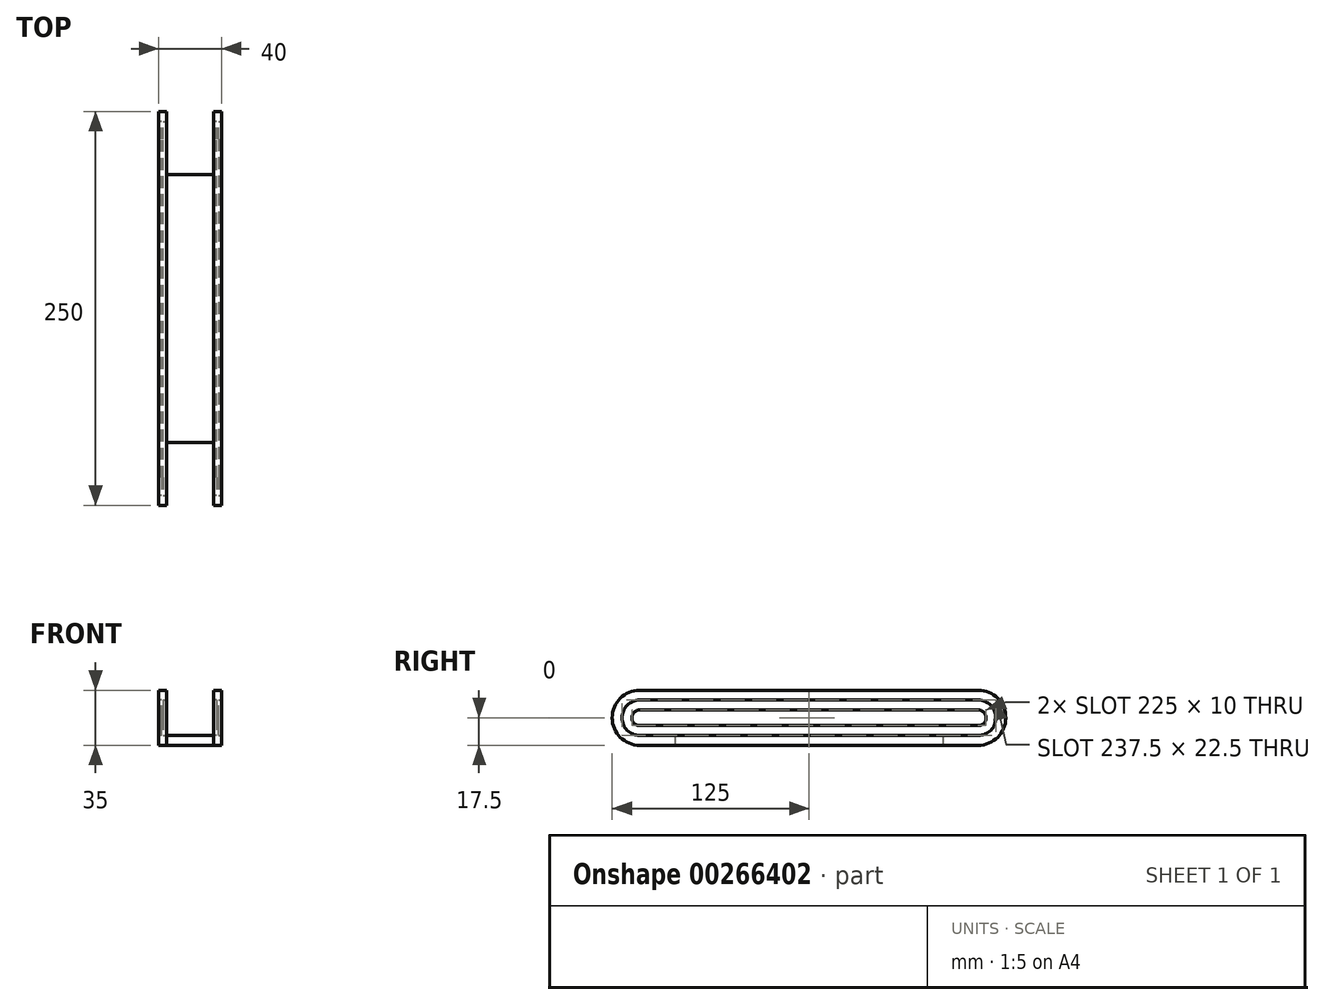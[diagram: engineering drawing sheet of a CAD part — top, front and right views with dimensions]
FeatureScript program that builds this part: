
annotation { "Feature Type Name" : "Feature", "Feature Type Description" : "" }
export const myFeature = defineFeature(function(context is Context, id is Id, definition is map)
    precondition{}
    {
        {
            var Q0;
            Q0=qCreatedBy(makeId("Front.planeOp"),FACE);
            var sketch = newSketch(context, id + "F0", { "sketchPlane" : qUnion([Q0])});
            skLineSegment(sketch, "E0.bottom", {"start": v(20, -17.5) * mm, "end": v(-20, -17.5) * mm});
            skLineSegment(sketch, "E0.left", {"start": v(20, -17.5) * mm, "end": v(20, 17.5) * mm});
            skLineSegment(sketch, "E0.right", {"start": v(-20, -17.5) * mm, "end": v(-20, 17.5) * mm});
            skPoint(sketch, "E0.middle", {"position": v(0, 0) * mm});
            skLineSegment(sketch, "E1", {"start": v(-20, 17.5) * mm, "end": v(-15, 17.5) * mm});
            skLineSegment(sketch, "E2", {"start": v(20, 17.5) * mm, "end": v(15, 17.5) * mm});
            skLineSegment(sketch, "E3", {"start": v(-15, 17.5) * mm, "end": v(-15, -11.25) * mm});
            skLineSegment(sketch, "E4", {"start": v(-15, -11.25) * mm, "end": v(15, -11.25) * mm});
            skLineSegment(sketch, "E5", {"start": v(15, -11.25) * mm, "end": v(15, 17.5) * mm});
            skSolve(sketch);
        }
        {
            var Q0;
            Q0=makeQuery(id+"F0.imprint","IMPRINT",FACE,{"disambiguationData":[TD([[makeQuery(id+"F0.imprint","IMPRINT",EDGE,{"derivedFrom":sQuery(id+"F0.wireOp",EDGE,"E0.bottom")}),-1.0]])]});
            extrude(context, id + "F1", {"entities" : qUnion([Q0]), "depth" : 125 * mm, "hasSecondDirection" : true, "secondDirectionOppositeDirection" : true, "secondDirectionDepth" : 125 * mm});
        }
        {
            var Q0;
            Q0=makeQuery(id+"F1.opExtrude","SWEPT_FACE",FACE,{"disambiguationData":[OSD([sQuery(id+"F0.wireOp",EDGE,"E3")])]});
            var sketch = newSketch(context, id + "F2", { "sketchPlane" : qUnion([Q0])});
            skLineSegment(sketch, "E6", {"start": v(0, 11.25) * mm, "end": v(-107.5, 11.25) * mm});
            skLineSegment(sketch, "E7", {"start": v(0, 5) * mm, "end": v(-107.5, 5) * mm});
            skLineSegment(sketch, "E8", {"start": v(0, -11.25) * mm, "end": v(-107.5, -11.25) * mm});
            skLineSegment(sketch, "E9", {"start": v(0, -5) * mm, "end": v(-107.5, -5) * mm});
            skArc(sketch, "E10", {"start": v(-107.5, 11.25) * mm, "mid": v(-118.75, 0) * mm, "end": v(-107.5, -11.25) * mm});
            skArc(sketch, "E11", {"start": v(-107.5, 5) * mm, "mid": v(-112.5, 0) * mm, "end": v(-107.5, -5) * mm});
            skLineSegment(sketch, "E12", {"start": v(0, 11.25) * mm, "end": v(107.5, 11.25) * mm});
            skLineSegment(sketch, "E13", {"start": v(0, -11.25) * mm, "end": v(107.5, -11.25) * mm});
            skLineSegment(sketch, "E14", {"start": v(0, -5) * mm, "end": v(107.5, -5) * mm});
            skLineSegment(sketch, "E15", {"start": v(0, 5) * mm, "end": v(107.5, 5) * mm});
            skArc(sketch, "E16", {"start": v(107.5, -11.25) * mm, "mid": v(118.75, 0) * mm, "end": v(107.5, 11.25) * mm});
            skArc(sketch, "E17", {"start": v(107.5, -5) * mm, "mid": v(112.5, 0) * mm, "end": v(107.5, 5) * mm});
            skSolve(sketch);
        }
        {
            var Q0;
            Q0=makeQuery(id+"F1.opExtrude","SWEPT_FACE",FACE,{"disambiguationData":[OSD([sQuery(id+"F0.wireOp",EDGE,"E5")])]});
            var sketch = newSketch(context, id + "F3", { "sketchPlane" : qUnion([Q0])});
            skPoint(sketch, "E18.endSnap0", {"position": v(0, 17.5) * mm});
            skPoint(sketch, "E19.endSnap0", {"position": v(0, -11.25) * mm});
            skLineSegment(sketch, "E20", {"start": v(0, 5) * mm, "end": v(-107.5, 5) * mm});
            skLineSegment(sketch, "E21", {"start": v(0, -5) * mm, "end": v(-107.5, -5) * mm});
            skLineSegment(sketch, "E22", {"start": v(0, 5) * mm, "end": v(107.5, 5) * mm});
            skLineSegment(sketch, "E23", {"start": v(0, -5) * mm, "end": v(107.5, -5) * mm});
            skLineSegment(sketch, "E24", {"start": v(0, 11.25) * mm, "end": v(107.5, 11.25) * mm});
            skLineSegment(sketch, "E25", {"start": v(0, -11.25) * mm, "end": v(107.5, -11.25) * mm});
            skLineSegment(sketch, "E26", {"start": v(0, 11.25) * mm, "end": v(-107.5, 11.25) * mm});
            skLineSegment(sketch, "E27", {"start": v(0, -11.25) * mm, "end": v(-107.5, -11.25) * mm});
            skArc(sketch, "E28", {"start": v(-107.5, 5) * mm, "mid": v(-112.5, 0) * mm, "end": v(-107.5, -5) * mm});
            skArc(sketch, "E29", {"start": v(-107.5, 11.25) * mm, "mid": v(-118.75, 0) * mm, "end": v(-107.5, -11.25) * mm});
            skPoint(sketch, "E30.end.orphan", {"position": v(125, 3.13) * mm});
            skPoint(sketch, "E30.start.orphan", {"position": v(0, 0) * mm});
            skArc(sketch, "E31", {"start": v(107.5, -5) * mm, "mid": v(112.5, 0) * mm, "end": v(107.5, 5) * mm});
            skArc(sketch, "E32", {"start": v(107.5, -11.25) * mm, "mid": v(118.75, 0) * mm, "end": v(107.5, 11.25) * mm});
            skPoint(sketch, "E19.start.orphan", {"position": v(0, -11.25) * mm});
            skSolve(sketch);
        }
        {
            var Q0;
            Q0=makeQuery(id+"F1.opExtrude","SWEPT_FACE",FACE,{"disambiguationData":[OSD([sQuery(id+"F0.wireOp",EDGE,"E0.right")])]});
            var sketch = newSketch(context, id + "F4", { "sketchPlane" : qUnion([Q0])});
            skPoint(sketch, "E33.endSnap0", {"position": v(0, 17.5) * mm});
            skLineSegment(sketch, "E34", {"start": v(0, 11.25) * mm, "end": v(-107.5, 11.25) * mm});
            skLineSegment(sketch, "E35", {"start": v(0, -11.25) * mm, "end": v(-107.5, -11.25) * mm});
            skLineSegment(sketch, "E36", {"start": v(0, 5) * mm, "end": v(-107.5, 5) * mm});
            skLineSegment(sketch, "E37", {"start": v(0, -5) * mm, "end": v(-107.5, -5) * mm});
            skLineSegment(sketch, "E38", {"start": v(0, 11.25) * mm, "end": v(107.5, 11.25) * mm});
            skLineSegment(sketch, "E39", {"start": v(0, 5) * mm, "end": v(107.5, 5) * mm});
            skLineSegment(sketch, "E40", {"start": v(0, -5) * mm, "end": v(107.5, -5) * mm});
            skLineSegment(sketch, "E41", {"start": v(0, -11.25) * mm, "end": v(107.5, -11.25) * mm});
            skArc(sketch, "E42", {"start": v(107.5, -5) * mm, "mid": v(112.5, 0) * mm, "end": v(107.5, 5) * mm});
            skArc(sketch, "E43", {"start": v(107.5, -11.25) * mm, "mid": v(118.75, 0) * mm, "end": v(107.5, 11.25) * mm});
            skArc(sketch, "E44", {"start": v(-107.5, 5) * mm, "mid": v(-112.5, 0) * mm, "end": v(-107.5, -5) * mm});
            skArc(sketch, "E45", {"start": v(-107.5, 11.25) * mm, "mid": v(-118.75, 0) * mm, "end": v(-107.5, -11.25) * mm});
            skPoint(sketch, "E46.orphan", {"position": v(-125, 0) * mm});
            skPoint(sketch, "E47.orphan", {"position": v(-125, -5) * mm});
            skPoint(sketch, "E48.start.orphan", {"position": v(-125, 5) * mm});
            skPoint(sketch, "E49.orphan", {"position": v(125, 0) * mm});
            skPoint(sketch, "E50.end.orphan", {"position": v(125, -5) * mm});
            skPoint(sketch, "E51.orphan", {"position": v(125, 5) * mm});
            skSolve(sketch);
        }
        {
            var Q0;
            Q0=makeQuery(id+"F1.opExtrude","SWEPT_FACE",FACE,{"disambiguationData":[OSD([sQuery(id+"F0.wireOp",EDGE,"E0.left")])]});
            var sketch = newSketch(context, id + "F5", { "sketchPlane" : qUnion([Q0])});
            skLineSegment(sketch, "E52", {"start": v(0, 11.25) * mm, "end": v(-107.5, 11.25) * mm});
            skLineSegment(sketch, "E53", {"start": v(0, -11.25) * mm, "end": v(-107.5, -11.25) * mm});
            skLineSegment(sketch, "E54", {"start": v(0, 11.25) * mm, "end": v(107.5, 11.25) * mm});
            skLineSegment(sketch, "E55", {"start": v(0, -11.25) * mm, "end": v(107.5, -11.25) * mm});
            skLineSegment(sketch, "E56", {"start": v(0, 5) * mm, "end": v(107.5, 5) * mm});
            skLineSegment(sketch, "E57", {"start": v(0, -5) * mm, "end": v(107.5, -5) * mm});
            skLineSegment(sketch, "E58", {"start": v(0, 5) * mm, "end": v(-107.5, 5) * mm});
            skLineSegment(sketch, "E59", {"start": v(0, -5) * mm, "end": v(-107.5, -5) * mm});
            skArc(sketch, "E60", {"start": v(107.5, -5) * mm, "mid": v(112.5, 0) * mm, "end": v(107.5, 5) * mm});
            skArc(sketch, "E61", {"start": v(107.5, -11.25) * mm, "mid": v(118.75, 0) * mm, "end": v(107.5, 11.25) * mm});
            skArc(sketch, "E62", {"start": v(-107.5, 5) * mm, "mid": v(-112.5, 0) * mm, "end": v(-107.5, -5) * mm});
            skArc(sketch, "E63", {"start": v(-107.5, 11.25) * mm, "mid": v(-118.75, 0) * mm, "end": v(-107.5, -11.25) * mm});
            skPoint(sketch, "E64.orphan", {"position": v(-125, 5) * mm});
            skPoint(sketch, "E65.start.orphan", {"position": v(-125, 0) * mm});
            skPoint(sketch, "E66.orphan", {"position": v(-125, -5) * mm});
            skPoint(sketch, "E67.start.orphan", {"position": v(0, 17.5) * mm});
            skPoint(sketch, "E68.start.orphan", {"position": v(125, 2.5) * mm});
            skPoint(sketch, "E69.orphan", {"position": v(125, 7.5) * mm});
            skPoint(sketch, "E70.end.orphan", {"position": v(125, -2.5) * mm});
            skSolve(sketch);
        }
        {
            var Q0;
            Q0=makeQuery(id+"F3.imprint","IMPRINT",FACE,{"disambiguationData":[TD([[makeQuery(id+"F3.imprint","IMPRINT",EDGE,{"derivedFrom":sQuery(id+"F3.wireOp",EDGE,"E20")}),1.0]])]});
            extrude(context, id + "F6", {"entities" : qUnion([Q0]), "operationType" : NewBodyOperationType.REMOVE, "endBound" : BoundingType.THROUGH_ALL, "oppositeDirection" : true, "depth" : 25 * mm});
        }
        {
            var Q0;
            Q0=makeQuery(id+"F2.imprint","IMPRINT",FACE,{"disambiguationData":[TD([[makeQuery(id+"F2.imprint","IMPRINT",EDGE,{"derivedFrom":sQuery(id+"F2.wireOp",EDGE,"E7")}),1.0]])]});
            extrude(context, id + "F7", {"entities" : qUnion([Q0]), "operationType" : NewBodyOperationType.REMOVE, "endBound" : BoundingType.THROUGH_ALL, "oppositeDirection" : true, "depth" : 25 * mm});
        }
        {
            var Q0;
            Q0=makeQuery(id+"F3.imprint","IMPRINT",FACE,{"disambiguationData":[TD([[makeQuery(id+"F3.imprint","IMPRINT",EDGE,{"derivedFrom":sQuery(id+"F3.wireOp",EDGE,"E20")}),-1.0]])]});
            extrude(context, id + "F8", {"entities" : qUnion([Q0]), "operationType" : NewBodyOperationType.REMOVE, "oppositeDirection" : true, "depth" : 2 * mm});
        }
        {
            var Q0;
            Q0=makeQuery(id+"F2.imprint","IMPRINT",FACE,{"disambiguationData":[TD([[makeQuery(id+"F2.imprint","IMPRINT",EDGE,{"derivedFrom":sQuery(id+"F2.wireOp",EDGE,"E6")}),1.0]])]});
            extrude(context, id + "F9", {"entities" : qUnion([Q0]), "operationType" : NewBodyOperationType.REMOVE, "oppositeDirection" : true, "depth" : 2 * mm});
        }
        {
            var Q0;
            Q0=makeQuery(id+"F4.imprint","IMPRINT",FACE,{"disambiguationData":[TD([[makeQuery(id+"F4.imprint","IMPRINT",EDGE,{"derivedFrom":sQuery(id+"F4.wireOp",EDGE,"E34")}),1.0]])]});
            extrude(context, id + "F10", {"entities" : qUnion([Q0]), "operationType" : NewBodyOperationType.REMOVE, "oppositeDirection" : true, "depth" : 2 * mm});
        }
        {
            var Q0;
            Q0=makeQuery(id+"F5.imprint","IMPRINT",FACE,{"disambiguationData":[TD([[makeQuery(id+"F5.imprint","IMPRINT",EDGE,{"derivedFrom":sQuery(id+"F5.wireOp",EDGE,"E52")}),1.0]])]});
            extrude(context, id + "F11", {"entities" : qUnion([Q0]), "operationType" : NewBodyOperationType.REMOVE, "oppositeDirection" : true, "depth" : 2 * mm});
        }
        {
            var Q0;
            Q0=makeQuery(id+"F1.opExtrude","SWEPT_FACE",FACE,{"disambiguationData":[OSD([sQuery(id+"F0.wireOp",EDGE,"E0.bottom")])]});
            var sketch = newSketch(context, id + "F12", { "sketchPlane" : qUnion([Q0])});
            skLineSegment(sketch, "E71", {"start": v(-15, 125) * mm, "end": v(15, 125) * mm});
            skLineSegment(sketch, "E72", {"start": v(-15, 125) * mm, "end": v(-15, 85) * mm});
            skLineSegment(sketch, "E73", {"start": v(-15, 85) * mm, "end": v(15, 85) * mm});
            skLineSegment(sketch, "E74", {"start": v(15, 85) * mm, "end": v(15, 125) * mm});
            skLineSegment(sketch, "E75", {"start": v(-15, -125) * mm, "end": v(15, -125) * mm});
            skLineSegment(sketch, "E76", {"start": v(-15, -125) * mm, "end": v(-15, -85) * mm});
            skLineSegment(sketch, "E77", {"start": v(-15, -85) * mm, "end": v(15, -85) * mm});
            skLineSegment(sketch, "E78", {"start": v(15, -85) * mm, "end": v(15, -125) * mm});
            skSolve(sketch);
        }
        {
            var Q0;
            Q0=makeQuery(id+"F12.imprint","IMPRINT",FACE,{"disambiguationData":[TD([[makeQuery(id+"F12.imprint","IMPRINT",EDGE,{"derivedFrom":sQuery(id+"F12.wireOp",EDGE,"E75")}),-1.0]])]});
            var Q1;
            Q1=makeQuery(id+"F12.imprint","IMPRINT",FACE,{"disambiguationData":[TD([[makeQuery(id+"F12.imprint","IMPRINT",EDGE,{"derivedFrom":sQuery(id+"F12.wireOp",EDGE,"E71")}),1.0]])]});
            extrude(context, id + "F13", {"entities" : qUnion([Q0, Q1]), "operationType" : NewBodyOperationType.REMOVE, "endBound" : BoundingType.THROUGH_ALL, "oppositeDirection" : true, "depth" : 25 * mm});
        }
        {
            var Q0;
            Q0=makeQuery(id+"F1.opExtrude","CAP_EDGE",EDGE,{"disambiguationData":[OSD([sQuery(id+"F0.wireOp",EDGE,"E2")])],"isStart":true});
            var Q1;
            {var subQ1=sQuery(id+"F0.wireOp",EDGE,"E0.left");var subQ2=sQuery(id+"F0.wireOp",EDGE,"E0.bottom");Q1=makeQuery(id+"F13.boolean.opBoolean","SPLIT",EDGE,{"disambiguationData":[TD([makeQuery(id+"F1.opExtrude","SWEPT_FACE",FACE,{"disambiguationData":[OSD([subQ1])]})])],"derivedFrom":makeQuery(id+"F1.opExtrude","CAP_EDGE",EDGE,{"disambiguationData":[OSD([subQ2])],"isStart":true})});}
            var Q2;
            {var subQ1=sQuery(id+"F0.wireOp",EDGE,"E0.right");var subQ2=sQuery(id+"F0.wireOp",EDGE,"E0.bottom");Q2=makeQuery(id+"F13.boolean.opBoolean","SPLIT",EDGE,{"disambiguationData":[TD([makeQuery(id+"F1.opExtrude","SWEPT_FACE",FACE,{"disambiguationData":[OSD([subQ1])]})])],"derivedFrom":makeQuery(id+"F1.opExtrude","CAP_EDGE",EDGE,{"disambiguationData":[OSD([subQ2])],"isStart":true})});}
            var Q3;
            Q3=makeQuery(id+"F1.opExtrude","CAP_EDGE",EDGE,{"disambiguationData":[OSD([sQuery(id+"F0.wireOp",EDGE,"E1")])],"isStart":true});
            var Q4;
            {var subQ0=sQuery(id+"F0.wireOp",EDGE,"E0.right");var subQ2=sQuery(id+"F0.wireOp",EDGE,"E0.bottom");Q4=makeQuery(id+"F13.boolean.opBoolean","SPLIT",EDGE,{"disambiguationData":[TD([makeQuery(id+"F1.opExtrude","SWEPT_FACE",FACE,{"disambiguationData":[OSD([subQ0])]})])],"derivedFrom":makeQuery(id+"F1.opExtrude","CAP_EDGE",EDGE,{"disambiguationData":[OSD([subQ2])],"isStart":false})});}
            var Q5;
            Q5=makeQuery(id+"F1.opExtrude","CAP_EDGE",EDGE,{"disambiguationData":[OSD([sQuery(id+"F0.wireOp",EDGE,"E1")])],"isStart":false});
            var Q6;
            Q6=makeQuery(id+"F1.opExtrude","CAP_EDGE",EDGE,{"disambiguationData":[OSD([sQuery(id+"F0.wireOp",EDGE,"E2")])],"isStart":false});
            var Q7;
            {var subQ1=sQuery(id+"F0.wireOp",EDGE,"E0.left");var subQ2=sQuery(id+"F0.wireOp",EDGE,"E0.bottom");Q7=makeQuery(id+"F13.boolean.opBoolean","SPLIT",EDGE,{"disambiguationData":[TD([makeQuery(id+"F1.opExtrude","SWEPT_FACE",FACE,{"disambiguationData":[OSD([subQ1])]})])],"derivedFrom":makeQuery(id+"F1.opExtrude","CAP_EDGE",EDGE,{"disambiguationData":[OSD([subQ2])],"isStart":false})});}
            fillet(context, id + "F14", {"entities" : qUnion([Q0, Q1, Q2, Q3, Q4, Q5, Q6, Q7]), "radius" : 17.5 * mm, "tangentPropagation" : true, "allowEdgeOverflow" : false});
        }
    });
